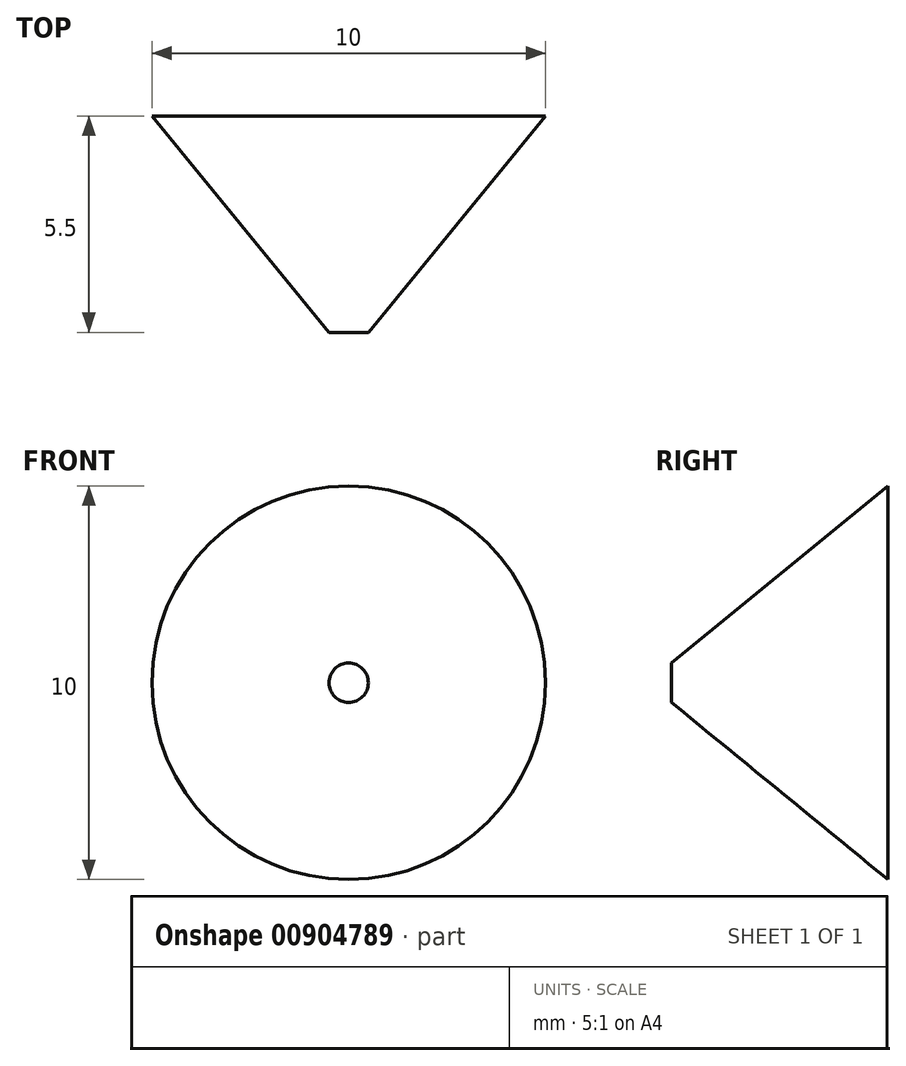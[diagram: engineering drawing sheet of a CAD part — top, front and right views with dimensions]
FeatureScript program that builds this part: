
annotation { "Feature Type Name" : "Feature", "Feature Type Description" : "" }
export const myFeature = defineFeature(function(context is Context, id is Id, definition is map)
    precondition{}
    {
        {
            var Q0;
            Q0=qCreatedBy(makeId("Front.planeOp"),FACE);
            var sketch = newSketch(context, id + "F0", { "sketchPlane" : qUnion([Q0])});
            skCircle(sketch, "E0", {"center": v(0, 0) * mm, "radius": 5 * mm});
            skSolve(sketch);
        }
        {
            var Q0;
            Q0=qCreatedBy(makeId("Front.planeOp"),FACE);
            cPlane(context, id + "F1", {"entities" : qUnion([Q0]), "cplaneType" : CPlaneType.OFFSET, "offset" : 5.5 * mm, "width" : 150 * mm, "height" : 150 * mm});
        }
        {
            var Q0;
            Q0=qCreatedBy(id+"F1.planeOp",FACE);
            var sketch = newSketch(context, id + "F2", { "sketchPlane" : qUnion([Q0])});
            skCircle(sketch, "E1", {"center": v(0, 0) * mm, "radius": 0.5 * mm});
            skSolve(sketch);
        }
        {
            var Q0;
            Q0=makeQuery(id+"F2.imprint","IMPRINT",FACE,{"disambiguationData":[TD([[makeQuery(id+"F2.imprint","IMPRINT",EDGE,{"derivedFrom":sQuery(id+"F2.wireOp",EDGE,"E1")}),1.0]])]});
            var Q1;
            Q1=makeQuery(id+"F0.imprint","IMPRINT",FACE,{"disambiguationData":[TD([[makeQuery(id+"F0.imprint","IMPRINT",EDGE,{"derivedFrom":sQuery(id+"F0.wireOp",EDGE,"E0")}),1.0]])]});
            loft(context, id + "F3", {"sheetProfilesArray" : [{ "sheetProfileEntities" : qUnion([Q0]) }, { "sheetProfileEntities" : qUnion([Q1]) }]});
        }
    });
